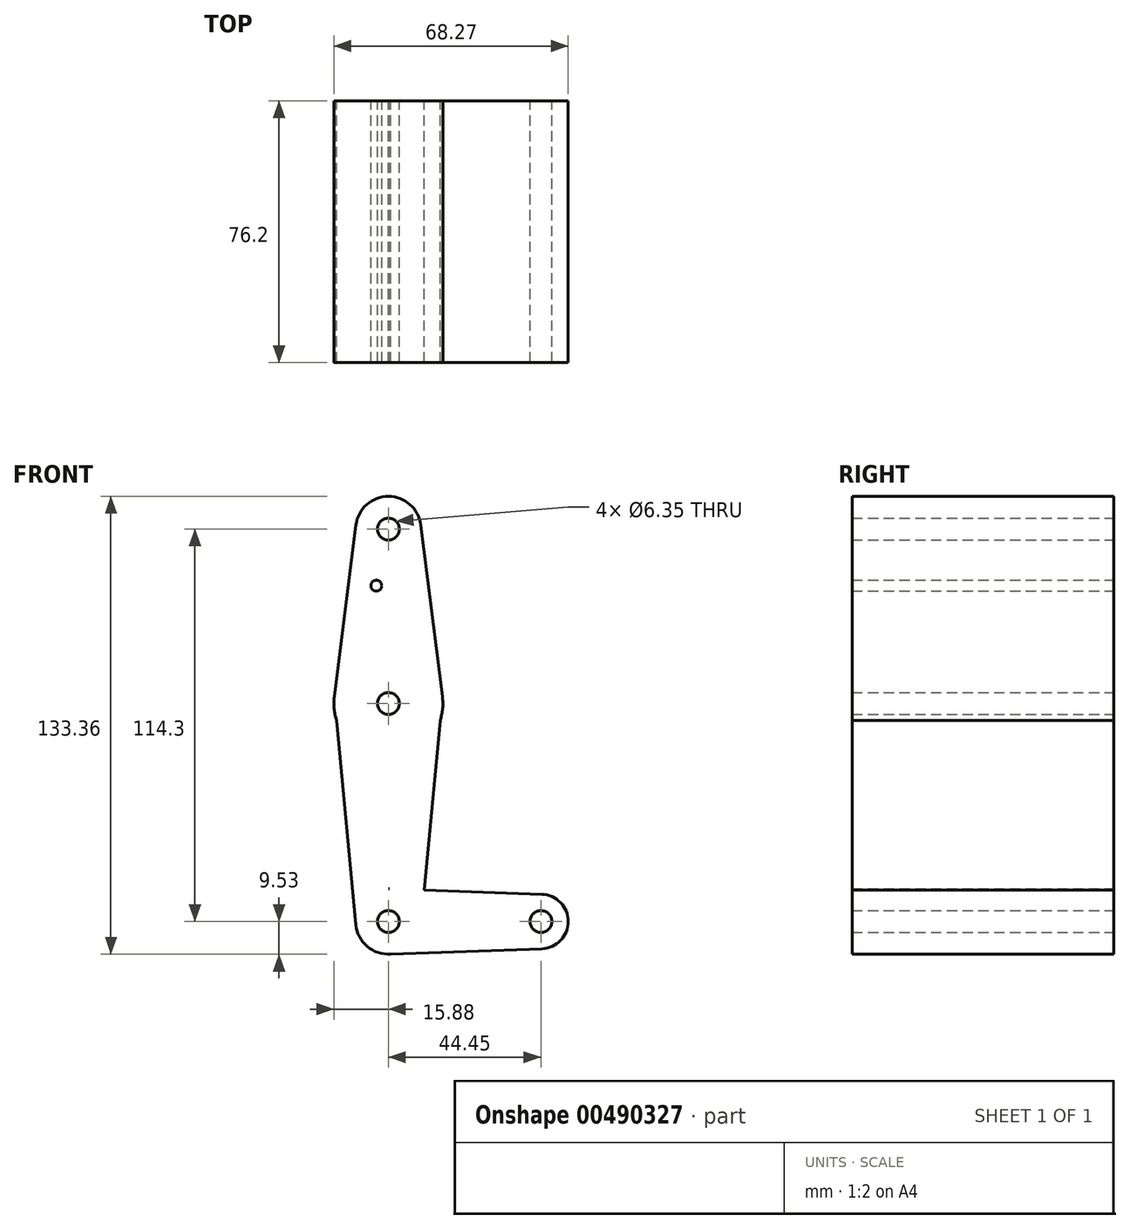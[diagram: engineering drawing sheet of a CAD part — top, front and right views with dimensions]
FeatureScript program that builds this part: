
annotation { "Feature Type Name" : "Feature", "Feature Type Description" : "" }
export const myFeature = defineFeature(function(context is Context, id is Id, definition is map)
    precondition{}
    {
        {
            var Q0;
            Q0=qCreatedBy(makeId("Front.planeOp"),FACE);
            var sketch = newSketch(context, id + "F0", { "sketchPlane" : qUnion([Q0])});
            skLineSegment(sketch, "E0", {"start": v(0, 0) * mm, "end": v(0, 114.3) * mm});
            skLineSegment(sketch, "E1", {"start": v(0, 114.3) * mm, "end": v(0, 0) * mm, "construction": true});
            skLineSegment(sketch, "E2", {"start": v(44.45, 0) * mm, "end": v(0, 0) * mm, "construction": true});
            skCircle(sketch, "E3", {"center": v(44.45, 0) * mm, "radius": 7.94 * mm});
            skCircle(sketch, "E4", {"center": v(0, 114.3) * mm, "radius": 9.53 * mm});
            skCircle(sketch, "E5", {"center": v(0, 0) * mm, "radius": 9.53 * mm});
            skCircle(sketch, "E6", {"center": v(0, 63.5) * mm, "radius": 15.88 * mm});
            skLineSegment(sketch, "E7", {"start": v(-9.45, 115.5) * mm, "end": v(-15.75, 65.48) * mm});
            skLineSegment(sketch, "E8", {"start": v(-15.75, 65.48) * mm, "end": v(-9.48, -0.9) * mm});
            skLineSegment(sketch, "E9", {"start": v(9.45, 115.5) * mm, "end": v(15.75, 65.48) * mm});
            skLineSegment(sketch, "E10", {"start": v(15.75, 65.48) * mm, "end": v(9.57, 0) * mm});
            skLineSegment(sketch, "E11", {"start": v(44.73, 7.93) * mm, "end": v(0, 9.53) * mm});
            skLineSegment(sketch, "E12", {"start": v(0, -9.53) * mm, "end": v(44.73, -7.93) * mm});
            skCircle(sketch, "E13", {"center": v(0, 114.3) * mm, "radius": 3.18 * mm});
            skCircle(sketch, "E14", {"center": v(0, 63.5) * mm, "radius": 3.18 * mm});
            skCircle(sketch, "E15", {"center": v(0, 0) * mm, "radius": 3.18 * mm});
            skCircle(sketch, "E16", {"center": v(44.45, 0) * mm, "radius": 3.18 * mm});
            skCircle(sketch, "E17", {"center": v(-3.52, 97.83) * mm, "radius": 1.59 * mm});
            skSolve(sketch);
        }
        {
            var Q0;
            Q0 = qSketchRegion(id + "F0", true);
            extrude(context, id + "F1", {"entities" : qUnion([Q0]), "depth" : 25.4 * mm});
        }
        {
            var Q0;
            Q0=makeQuery(id+"F1.opExtrude","CAP_FACE",FACE,{"disambiguationData":[OSD([sQuery(id+"F0.wireOp",EDGE,"E0"),sQuery(id+"F0.wireOp",EDGE,"E3"),sQuery(id+"F0.wireOp",EDGE,"E4"),sQuery(id+"F0.wireOp",EDGE,"E5"),sQuery(id+"F0.wireOp",EDGE,"E6"),sQuery(id+"F0.wireOp",EDGE,"E7"),sQuery(id+"F0.wireOp",EDGE,"E8"),sQuery(id+"F0.wireOp",EDGE,"E9"),sQuery(id+"F0.wireOp",EDGE,"E10"),sQuery(id+"F0.wireOp",EDGE,"E11"),sQuery(id+"F0.wireOp",EDGE,"E12"),sQuery(id+"F0.wireOp",EDGE,"E13"),sQuery(id+"F0.wireOp",EDGE,"E14"),sQuery(id+"F0.wireOp",EDGE,"E15"),sQuery(id+"F0.wireOp",EDGE,"E16"),sQuery(id+"F0.wireOp",EDGE,"E17")])],"isStart":false});
            extrude(context, id + "F2", {"entities" : qUnion([Q0]), "operationType" : NewBodyOperationType.ADD, "depth" : 25.4 * mm});
        }
        {
            var Q0;
            Q0=makeQuery(id+"F2.opExtrude","CAP_FACE",FACE,{"disambiguationData":[OSD([sQuery(id+"F0.wireOp",EDGE,"E0"),sQuery(id+"F0.wireOp",EDGE,"E3"),sQuery(id+"F0.wireOp",EDGE,"E4"),sQuery(id+"F0.wireOp",EDGE,"E5"),sQuery(id+"F0.wireOp",EDGE,"E6"),sQuery(id+"F0.wireOp",EDGE,"E7"),sQuery(id+"F0.wireOp",EDGE,"E8"),sQuery(id+"F0.wireOp",EDGE,"E9"),sQuery(id+"F0.wireOp",EDGE,"E10"),sQuery(id+"F0.wireOp",EDGE,"E11"),sQuery(id+"F0.wireOp",EDGE,"E12"),sQuery(id+"F0.wireOp",EDGE,"E13"),sQuery(id+"F0.wireOp",EDGE,"E14"),sQuery(id+"F0.wireOp",EDGE,"E15"),sQuery(id+"F0.wireOp",EDGE,"E16"),sQuery(id+"F0.wireOp",EDGE,"E17")])],"isStart":false});
            extrude(context, id + "F3", {"entities" : qUnion([Q0]), "operationType" : NewBodyOperationType.ADD, "depth" : 25.4 * mm});
        }
    });
